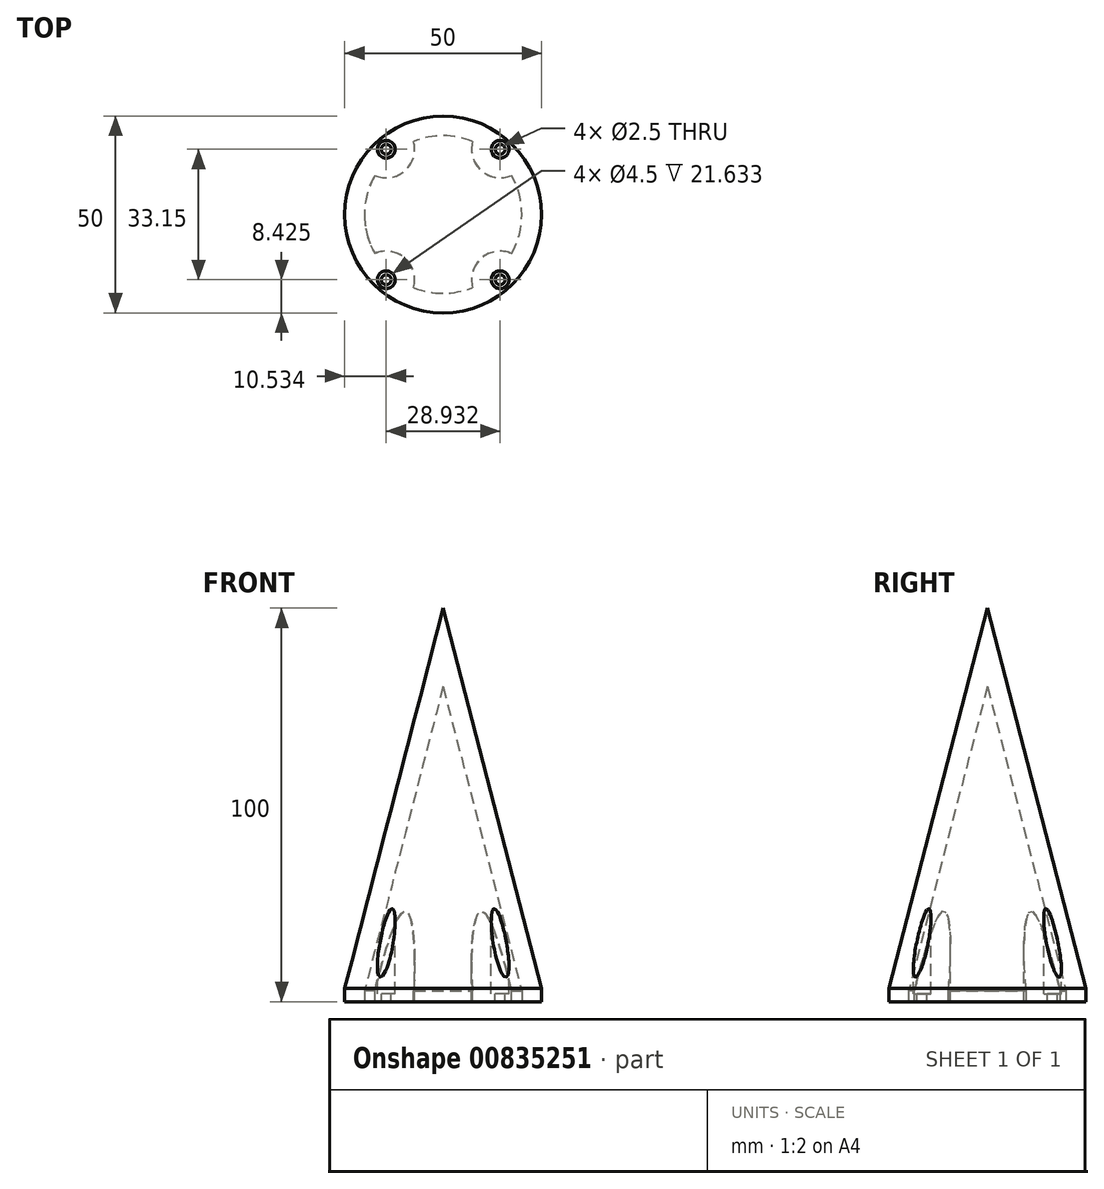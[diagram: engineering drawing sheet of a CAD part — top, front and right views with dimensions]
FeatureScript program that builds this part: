
annotation { "Feature Type Name" : "Feature", "Feature Type Description" : "" }
export const myFeature = defineFeature(function(context is Context, id is Id, definition is map)
    precondition{}
    {
        {
            var Q0;
            Q0=qCreatedBy(makeId("Top.planeOp"),FACE);
            var sketch = newSketch(context, id + "F0", { "sketchPlane" : qUnion([Q0])});
            skCircle(sketch, "E0", {"center": v(0, 0) * mm, "radius": 25 * mm});
            skSolve(sketch);
        }
        {
            var Q0;
            Q0=makeQuery(id+"F0.imprint","IMPRINT",FACE,{"disambiguationData":[TD([[makeQuery(id+"F0.imprint","IMPRINT",EDGE,{"derivedFrom":sQuery(id+"F0.wireOp",EDGE,"E0")}),1.0]])]});
            extrude(context, id + "F1", {"entities" : qUnion([Q0]), "depth" : 100 * mm, "offsetDistance" : 25 * mm});
        }
        {
            var Q0;
            Q0=makeQuery(id+"F1.opExtrude","CAP_FACE",FACE,{"disambiguationData":[OSD([sQuery(id+"F0.wireOp",EDGE,"E0")])],"isStart":false});
            var sketch = newSketch(context, id + "F2", { "sketchPlane" : qUnion([Q0])});
            skCircle(sketch, "E1", {"center": v(-14.47, -16.57) * mm, "radius": 3 * mm});
            skPoint(sketch, "E1.first.point", {"position": v(-16.44, -18.84) * mm});
            skPoint(sketch, "E1.second.point", {"position": v(-12.8, -14.08) * mm});
            skPoint(sketch, "E1.third.point", {"position": v(-15.23, -13.67) * mm});
            skCircle(sketch, "E2", {"center": v(-14.47, -16.57) * mm, "radius": 1.25 * mm});
            skCircle(sketch, "E3.MirrorC", {"center": v(-14.47, 16.57) * mm, "radius": 1.25 * mm});
            skCircle(sketch, "E4.MirrorC", {"center": v(-14.47, 16.57) * mm, "radius": 3 * mm});
            skCircle(sketch, "E5.MirrorC", {"center": v(14.47, -16.57) * mm, "radius": 1.25 * mm});
            skCircle(sketch, "E6.MirrorC", {"center": v(14.47, -16.57) * mm, "radius": 3 * mm});
            skCircle(sketch, "E7.MirrorC", {"center": v(14.47, 16.57) * mm, "radius": 3 * mm});
            skCircle(sketch, "E8.MirrorC", {"center": v(14.47, 16.57) * mm, "radius": 1.25 * mm});
            skSolve(sketch);
        }
        {
            var Q0;
            Q0=sQuery(id+"F2.wireOp",VERTEX,"E7.MirrorC.center");
            var Q1;
            Q1=sQuery(id+"F2.wireOp",VERTEX,"E5.MirrorC.center");
            var Q2;
            Q2=sQuery(id+"F2.wireOp",VERTEX,"E1.center");
            var Q3;
            Q3=sQuery(id+"F2.wireOp",VERTEX,"E3.MirrorC.center");
            var Q4;
            Q4=makeQuery(id+"F1.opExtrude","SWEPT_BODY",BODY,{"disambiguationData":[OSD([sQuery(id+"F0.wireOp",EDGE,"E0")])]});
            hole(context, id + "F3", {"style" : HoleStyle.C_BORE, "endStyle" : HoleEndStyle.THROUGH, "holeDiameter" : 2.5 * mm, "cBoreDiameter" : 4.5 * mm, "cBoreDepth" : 98 * mm, "majorDiameter" : 5 * mm, "isTappedThrough" : true, "tappedDepth" : 12 * mm, "tapClearance" : 3, "locations" : qUnion([Q0, Q1, Q2, Q3]), "scope" : qUnion([Q4])});
        }
        {
            var Q0;
            Q0=makeQuery(id+"F1.opExtrude","CAP_EDGE",EDGE,{"disambiguationData":[OSD([sQuery(id+"F0.wireOp",EDGE,"E0")])],"isStart":false});
            chamfer(context, id + "F4", {"entities" : qUnion([Q0]), "chamferType" : ChamferType.OFFSET_ANGLE, "width" : 25 * mm, "oppositeDirection" : false, "angle" : 75.5 * degree, "tangentPropagation" : true});
        }
        {
            var Q0;
            Q0=makeQuery(id+"F1.opExtrude","CAP_FACE",FACE,{"disambiguationData":[OSD([sQuery(id+"F0.wireOp",EDGE,"E0")])],"isStart":true});
            shell(context, id + "F5", {"entities" : qUnion([Q0]), "thickness" : 5 * mm});
        }
    });
